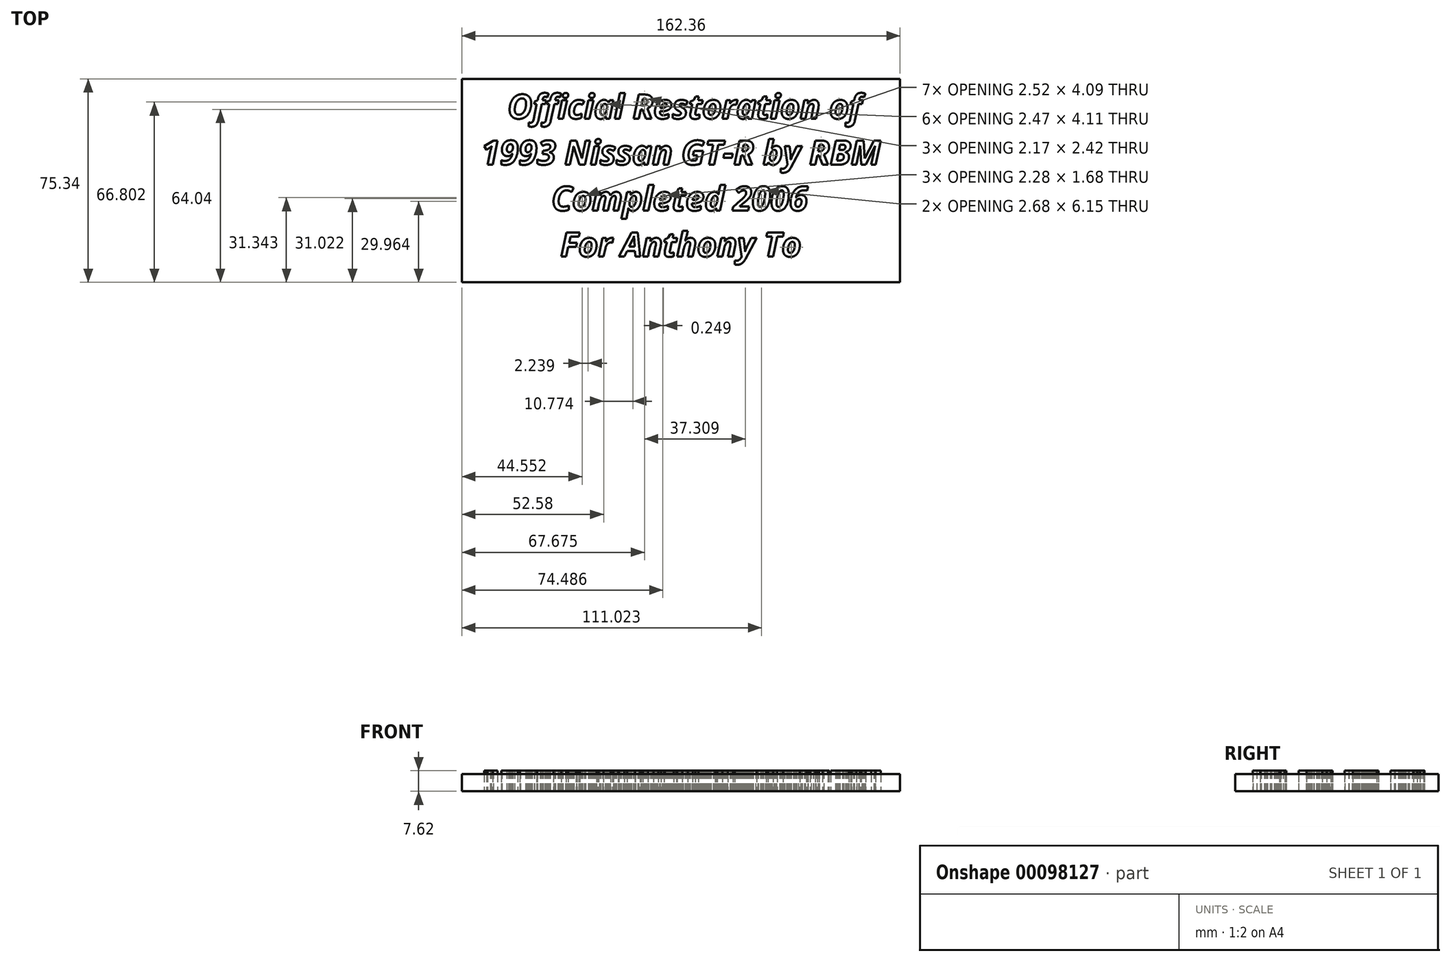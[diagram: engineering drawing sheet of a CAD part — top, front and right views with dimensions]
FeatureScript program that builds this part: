
annotation { "Feature Type Name" : "Feature", "Feature Type Description" : "" }
export const myFeature = defineFeature(function(context is Context, id is Id, definition is map)
    precondition{}
    {
        {
            var Q0;
            Q0=qCreatedBy(makeId("Top.planeOp"),FACE);
            var sketch = newSketch(context, id + "F0", { "sketchPlane" : qUnion([Q0])});
            skPoint(sketch, "E0.middle", {"position": v(0, 0) * mm});
            skText(sketch, "E1", { "text": "   Official Restoration of \n1993 Nissan GT-R by RBM\n        Completed 2006 \n         For Anthony To ", "fontName": "OpenSans-BoldItalic.ttf"});
            const initialGuessF0  = {"E1": [-0.074, 0.01747, 1, 0, 0.00902]};
            skSetInitialGuess(sketch, initialGuessF0);
            skSolve(sketch);
        }
        {
            var Q0;
            Q0=qCreatedBy(makeId("Top.planeOp"),FACE);
            var sketch = newSketch(context, id + "F1", { "sketchPlane" : qUnion([Q0])});
            skLineSegment(sketch, "E2.bottom", {"start": v(81.18, -43.15) * mm, "end": v(-81.18, -43.15) * mm});
            skLineSegment(sketch, "E2.top", {"start": v(81.18, 32.2) * mm, "end": v(-81.18, 32.2) * mm});
            skLineSegment(sketch, "E2.left", {"start": v(81.18, -43.15) * mm, "end": v(81.18, 32.2) * mm});
            skLineSegment(sketch, "E2.right", {"start": v(-81.18, -43.15) * mm, "end": v(-81.18, 32.2) * mm});
            skPoint(sketch, "E2.middle", {"position": v(0, -5.48) * mm});
            skSolve(sketch);
        }
        {
            var Q0;
            Q0 = qSketchRegion(id + "F0", true);
            extrude(context, id + "F2", {"entities" : qUnion([Q0]), "depth" : 7.62 * mm});
        }
        {
            var Q0;
            Q0 = qSketchRegion(id + "F1", true);
            extrude(context, id + "F3", {"entities" : qUnion([Q0]), "depth" : 6.35 * mm});
        }
    });
